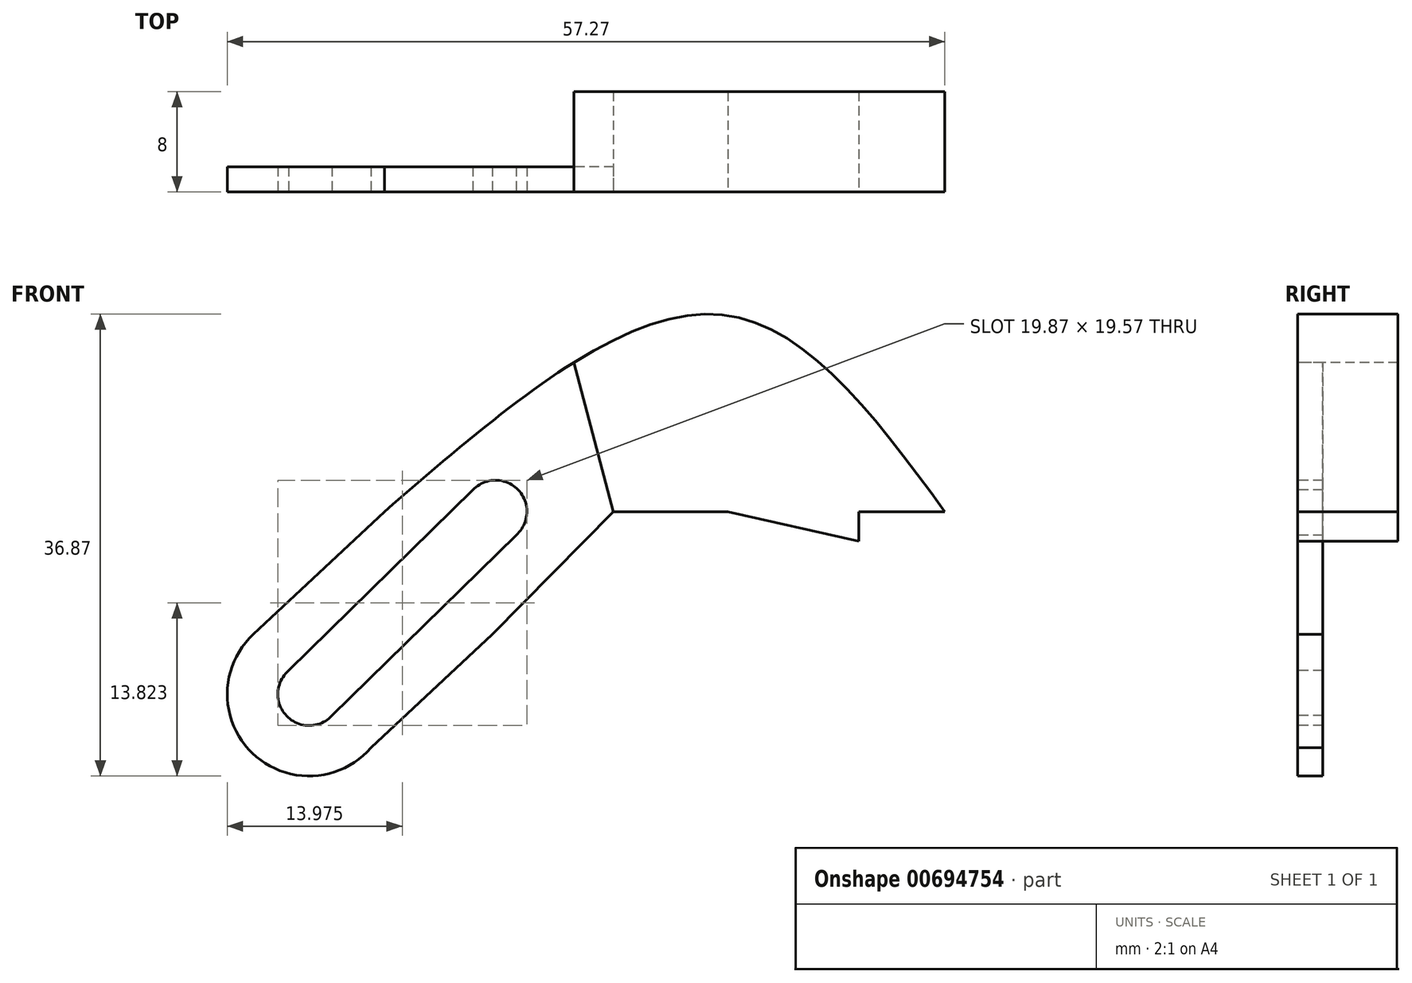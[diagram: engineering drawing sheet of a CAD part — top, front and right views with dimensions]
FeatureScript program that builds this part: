
annotation { "Feature Type Name" : "Feature", "Feature Type Description" : "" }
export const myFeature = defineFeature(function(context is Context, id is Id, definition is map)
    precondition{}
    {
        {
            var Q0;
            Q0=qCreatedBy(makeId("Front.planeOp"),FACE);
            var sketch = newSketch(context, id + "F0", { "sketchPlane" : qUnion([Q0])});
            skFitSpline(sketch, "E0", {"points": [v(0, 0) * mm, v(-17.86, 15.71) * mm, v(-44.72, 0) * mm], "startDerivative": vector(-35.48, 48.4) * mm, "endDerivative": vector(-53.56, -46.3) * mm});
            skLineSegment(sketch, "E1", {"start": v(0, 0) * mm, "end": v(0, -3.9) * mm});
            skLineSegment(sketch, "E2", {"start": v(0, -3.9) * mm, "end": v(-17.32, 0) * mm});
            skLineSegment(sketch, "E3", {"start": v(-17.32, 0) * mm, "end": v(-26.46, 0) * mm});
            skLineSegment(sketch, "E4", {"start": v(-26.46, 0) * mm, "end": v(-36.13, -9.8) * mm});
            skLineSegment(sketch, "E5", {"start": v(-44.72, 0) * mm, "end": v(-55.2, -9.8) * mm});
            skLineSegment(sketch, "E6", {"start": v(-36.13, -9.8) * mm, "end": v(-45.8, -18.86) * mm});
            skArc(sketch, "E7", {"start": v(-55.2, -9.8) * mm, "mid": v(-55.27, -19.28) * mm, "end": v(-45.8, -18.86) * mm});
            skPoint(sketch, "E8", {"position": v(-35.86, 0) * mm});
            skArc(sketch, "E9", {"start": v(-34.22, -1.89) * mm, "mid": v(-34.05, 1.73) * mm, "end": v(-37.67, 1.72) * mm});
            skArc(sketch, "E10", {"start": v(-52.38, -12.7) * mm, "mid": v(-52.53, -16.32) * mm, "end": v(-48.9, -16.28) * mm});
            skLineSegment(sketch, "E11", {"start": v(-52.38, -12.7) * mm, "end": v(-37.54, 1.85) * mm});
            skLineSegment(sketch, "E12", {"start": v(-34, -1.67) * mm, "end": v(-49.07, -16.44) * mm});
            skLineSegment(sketch, "E13", {"start": v(0, 0) * mm, "end": v(-6.87, 0) * mm});
            skLineSegment(sketch, "E14", {"start": v(-6.87, 0) * mm, "end": v(-6.87, -2.35) * mm});
            skLineSegment(sketch, "E15", {"start": v(-6.87, -2.35) * mm, "end": v(0, -3.9) * mm});
            skLineSegment(sketch, "E16", {"start": v(-26.46, 0) * mm, "end": v(-29.6, 11.9) * mm});
            skSolve(sketch);
        }
        {
            var Q0;
            Q0=makeQuery(id+"F0.imprint","IMPRINT",FACE,{"disambiguationData":[TD([[makeQuery(id+"F0.imprint","IMPRINT",EDGE,{"derivedFrom":sQuery(id+"F0.wireOp",EDGE,"E1")}),-1.0]])]});
            var Q1;
            Q1=makeQuery(id+"F0.imprint","IMPRINT",FACE,{"disambiguationData":[TD([[makeQuery(id+"F0.imprint","IMPRINT",EDGE,{"derivedFrom":sQuery(id+"F0.wireOp",EDGE,"E0")}),1.0]])]});
            extrude(context, id + "F1", {"entities" : qUnion([Q0, Q1]), "oppositeDirection" : true, "depth" : 8 * mm, "offsetDistance" : 25 * mm});
        }
        {
            var Q0;
            Q0=makeQuery(id+"F0.imprint","IMPRINT",FACE,{"disambiguationData":[TD([[makeQuery(id+"F0.imprint","IMPRINT",EDGE,{"derivedFrom":sQuery(id+"F0.wireOp",EDGE,"E4")}),-1.0]])]});
            extrude(context, id + "F2", {"entities" : qUnion([Q0]), "oppositeDirection" : true, "depth" : 2 * mm, "offsetDistance" : 25 * mm});
        }
        {
            var Q0;
            Q0=makeQuery(id+"F0.imprint","IMPRINT",FACE,{"disambiguationData":[TD([[makeQuery(id+"F0.imprint","IMPRINT",EDGE,{"derivedFrom":sQuery(id+"F0.wireOp",EDGE,"E1")}),-1.0]])]});
            extrude(context, id + "F3", {"entities" : qUnion([Q0]), "operationType" : NewBodyOperationType.REMOVE, "oppositeDirection" : true, "depth" : 25 * mm, "offsetDistance" : 25 * mm});
        }
    });
